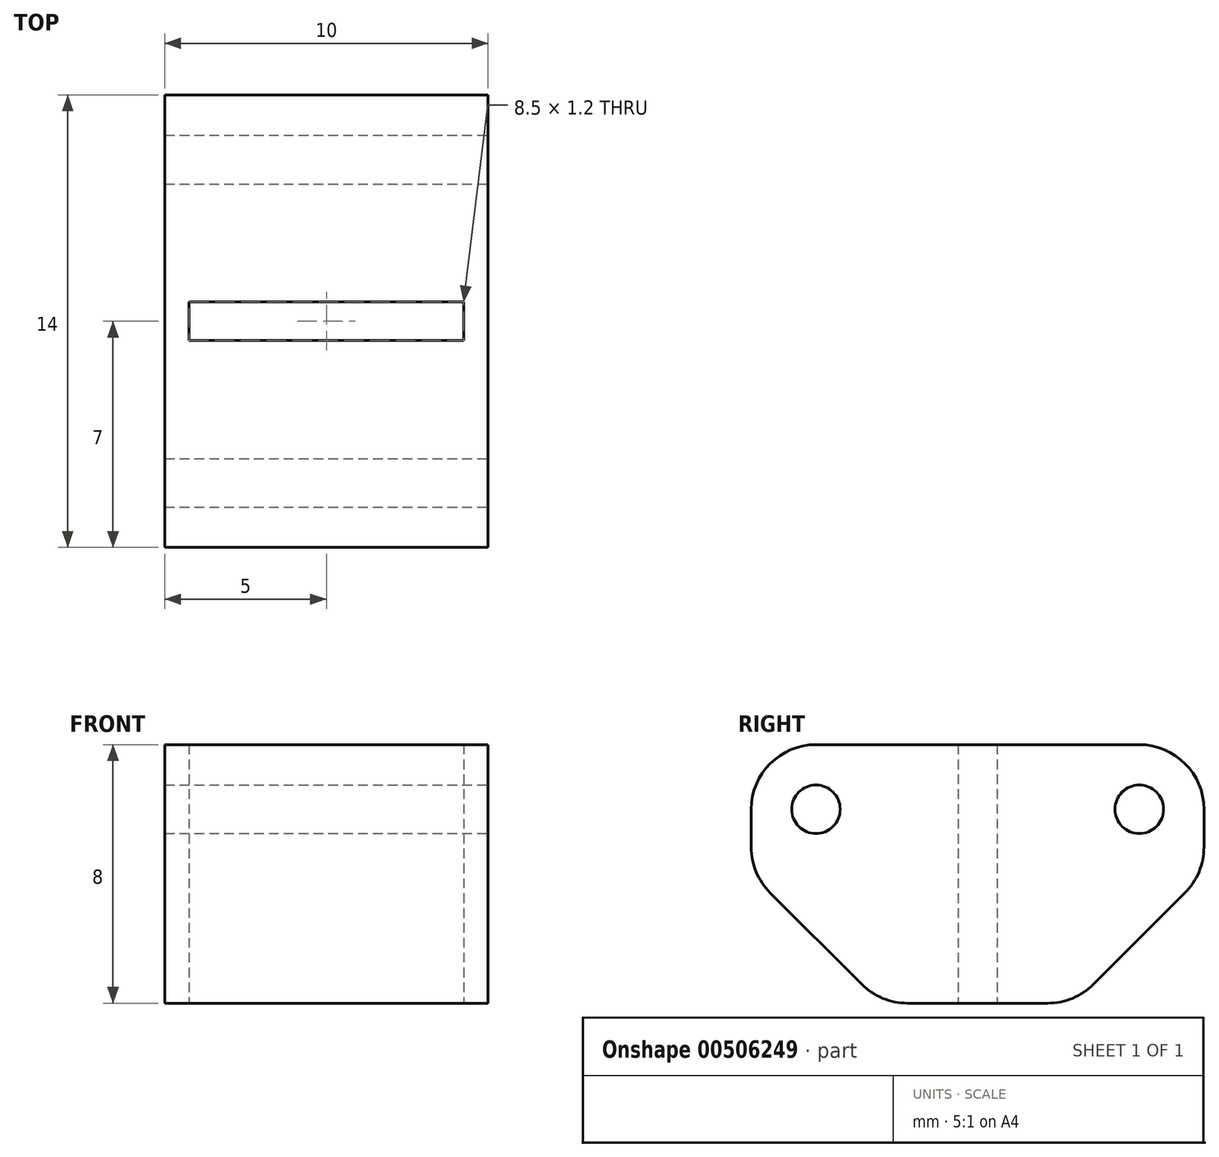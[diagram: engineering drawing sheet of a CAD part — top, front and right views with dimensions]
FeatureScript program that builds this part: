
annotation { "Feature Type Name" : "Feature", "Feature Type Description" : "" }
export const myFeature = defineFeature(function(context is Context, id is Id, definition is map)
    precondition{}
    {
        {
            var Q0;
            Q0=qCreatedBy(makeId("Top.planeOp"),FACE);
            var sketch = newSketch(context, id + "F0", { "sketchPlane" : qUnion([Q0])});
            skLineSegment(sketch, "E0.bottom", {"start": v(-5, 3) * mm, "end": v(5, 3) * mm});
            skLineSegment(sketch, "E0.top", {"start": v(-5, -3) * mm, "end": v(5, -3) * mm});
            skLineSegment(sketch, "E0.left", {"start": v(-5, 3) * mm, "end": v(-5, -3) * mm});
            skLineSegment(sketch, "E0.right", {"start": v(5, 3) * mm, "end": v(5, -3) * mm});
            skLineSegment(sketch, "E1.bottom", {"start": v(-4.25, 0.6) * mm, "end": v(4.25, 0.6) * mm});
            skLineSegment(sketch, "E1.top", {"start": v(-4.25, -0.6) * mm, "end": v(4.25, -0.6) * mm});
            skLineSegment(sketch, "E1.left", {"start": v(-4.25, 0.6) * mm, "end": v(-4.25, -0.6) * mm});
            skLineSegment(sketch, "E1.right", {"start": v(4.25, 0.6) * mm, "end": v(4.25, -0.6) * mm});
            skSolve(sketch);
        }
        {
            var Q0;
            Q0=makeQuery(id+"F0.imprint","IMPRINT",FACE,{"disambiguationData":[TD([[makeQuery(id+"F0.imprint","IMPRINT",EDGE,{"derivedFrom":sQuery(id+"F0.wireOp",EDGE,"E0.bottom")}),-1.0]])]});
            extrude(context, id + "F1", {"entities" : qUnion([Q0]), "depth" : 8 * mm});
        }
        {
            var Q0;
            Q0=makeQuery(id+"F1.opExtrude","SWEPT_FACE",FACE,{"disambiguationData":[OSD([sQuery(id+"F0.wireOp",EDGE,"E0.right")])]});
            var sketch = newSketch(context, id + "F2", { "sketchPlane" : qUnion([Q0])});
            skLineSegment(sketch, "E2.left", {"start": v(-3, 8) * mm, "end": v(-3, 8) * mm});
            skLineSegment(sketch, "E3.bottom", {"start": v(-3, 8) * mm, "end": v(-5, 8) * mm});
            skLineSegment(sketch, "E3.top", {"start": v(-3, 4) * mm, "end": v(-7, 4) * mm});
            skLineSegment(sketch, "E3.left", {"start": v(-3, 8) * mm, "end": v(-3, 4) * mm});
            skLineSegment(sketch, "E3.right", {"start": v(-7, 6) * mm, "end": v(-7, 4) * mm});
            skCircle(sketch, "E4", {"center": v(-5, 6) * mm, "radius": 0.75 * mm});
            skLineSegment(sketch, "E5.bottom", {"start": v(3, 8) * mm, "end": v(5, 8) * mm});
            skLineSegment(sketch, "E5.top", {"start": v(3, 4) * mm, "end": v(7, 4) * mm});
            skLineSegment(sketch, "E5.left", {"start": v(3, 8) * mm, "end": v(3, 4) * mm});
            skLineSegment(sketch, "E5.right", {"start": v(7, 6) * mm, "end": v(7, 4) * mm});
            skCircle(sketch, "E6", {"center": v(5, 6) * mm, "radius": 0.75 * mm});
            skPoint(sketch, "E7.visualSharp", {"position": v(-7, 8) * mm});
            skArc(sketch, "E7.filletArc", {"start": v(-5, 8) * mm, "mid": v(-6.41, 7.41) * mm, "end": v(-7, 6) * mm});
            skLineSegment(sketch, "E8", {"start": v(-7, 4) * mm, "end": v(-3, 0) * mm});
            skLineSegment(sketch, "E9", {"start": v(7, 4) * mm, "end": v(3, 0) * mm});
            skPoint(sketch, "E10.visualSharp", {"position": v(7, 8) * mm});
            skArc(sketch, "E10.filletArc", {"start": v(7, 6) * mm, "mid": v(6.41, 7.41) * mm, "end": v(5, 8) * mm});
            skSolve(sketch);
        }
        {
            var Q0;
            Q0=makeQuery(id+"F2.imprint","IMPRINT",FACE,{"disambiguationData":[TD([[makeQuery(id+"F2.imprint","IMPRINT",EDGE,{"derivedFrom":sQuery(id+"F2.wireOp",EDGE,"E3.bottom")}),1.0]])]});
            var Q1;
            {var subQ0=sQuery(id+"F2.wireOp",EDGE,"E3.top");Q1=makeQuery(id+"F2.imprint","IMPRINT",FACE,{"disambiguationData":[TD([[makeQuery(id+"F2.imprint","IMPRINT",EDGE,{"derivedFrom":subQ0}),1.0]])]});}
            var Q2;
            Q2=makeQuery(id+"F2.imprint","IMPRINT",FACE,{"disambiguationData":[TD([[makeQuery(id+"F2.imprint","IMPRINT",EDGE,{"derivedFrom":sQuery(id+"F2.wireOp",EDGE,"E5.bottom")}),-1.0]])]});
            var Q3;
            {var subQ0=sQuery(id+"F2.wireOp",EDGE,"E5.top");Q3=makeQuery(id+"F2.imprint","IMPRINT",FACE,{"disambiguationData":[TD([[makeQuery(id+"F2.imprint","IMPRINT",EDGE,{"derivedFrom":subQ0}),-1.0]])]});}
            extrude(context, id + "F3", {"entities" : qUnion([Q0, Q1, Q2, Q3]), "oppositeDirection" : true, "depth" : 10 * mm});
        }
        {
            var Q0;
            Q0=makeQuery(id+"F1.opExtrude","SWEPT_BODY",BODY,{"disambiguationData":[OSD([sQuery(id+"F0.wireOp",EDGE,"E0.bottom"),sQuery(id+"F0.wireOp",EDGE,"E0.top"),sQuery(id+"F0.wireOp",EDGE,"E0.left"),sQuery(id+"F0.wireOp",EDGE,"E0.right"),sQuery(id+"F0.wireOp",EDGE,"E1.bottom"),sQuery(id+"F0.wireOp",EDGE,"E1.top"),sQuery(id+"F0.wireOp",EDGE,"E1.left"),sQuery(id+"F0.wireOp",EDGE,"E1.right")])]});
            var Q1;
            Q1=makeQuery(id+"F3.opExtrude","SWEPT_BODY",BODY,{"disambiguationData":[OSD([sQuery(id+"F0.wireOp",EDGE,"E0.top"),sQuery(id+"F0.wireOp",EDGE,"E0.right"),sQuery(id+"F2.wireOp",EDGE,"E3.bottom"),sQuery(id+"F2.wireOp",EDGE,"E3.left"),sQuery(id+"F2.wireOp",EDGE,"E3.right"),sQuery(id+"F2.wireOp",EDGE,"E4"),sQuery(id+"F2.wireOp",EDGE,"E7.filletArc"),sQuery(id+"F2.wireOp",EDGE,"E8")])]});
            var Q2;
            Q2=makeQuery(id+"F3.opExtrude","SWEPT_BODY",BODY,{"disambiguationData":[OSD([sQuery(id+"F0.wireOp",EDGE,"E0.bottom"),sQuery(id+"F0.wireOp",EDGE,"E0.right"),sQuery(id+"F2.wireOp",EDGE,"E5.bottom"),sQuery(id+"F2.wireOp",EDGE,"E5.left"),sQuery(id+"F2.wireOp",EDGE,"E5.right"),sQuery(id+"F2.wireOp",EDGE,"E6"),sQuery(id+"F2.wireOp",EDGE,"E9"),sQuery(id+"F2.wireOp",EDGE,"E10.filletArc")])]});
            booleanBodies(context, id + "F4", {"operationType" : BooleanOperationType.UNION, "tools" : qUnion([Q0, Q1, Q2])});
        }
        {
            var Q0;
            {var subQ0=sQuery(id+"F0.wireOp",EDGE,"E0.bottom");Q0=makeQuery(id+"F4.opBoolean","MERGE",EDGE,{"derivedFrom":[makeQuery(id+"F1.opExtrude","CAP_EDGE",EDGE,{"disambiguationData":[OSD([subQ0])],"isStart":true}),makeQuery(id+"F3.opExtrude","SWEPT_EDGE",EDGE,{"disambiguationData":[OSD([subQ0,sQuery(id+"F0.wireOp",EDGE,"E0.right"),sQuery(id+"F2.wireOp",EDGE,"E9")])]})]});}
            var Q1;
            Q1=makeQuery(id+"F3.opExtrude","SWEPT_EDGE",EDGE,{"disambiguationData":[OSD([sQuery(id+"F2.wireOp",EDGE,"E5.top"),sQuery(id+"F2.wireOp",EDGE,"E5.right"),sQuery(id+"F2.wireOp",EDGE,"E9")])]});
            var Q2;
            {var subQ0=sQuery(id+"F0.wireOp",EDGE,"E0.top");Q2=makeQuery(id+"F4.opBoolean","MERGE",EDGE,{"derivedFrom":[makeQuery(id+"F1.opExtrude","CAP_EDGE",EDGE,{"disambiguationData":[OSD([subQ0])],"isStart":true}),makeQuery(id+"F3.opExtrude","SWEPT_EDGE",EDGE,{"disambiguationData":[OSD([subQ0,sQuery(id+"F0.wireOp",EDGE,"E0.right"),sQuery(id+"F2.wireOp",EDGE,"E8")])]})]});}
            var Q3;
            Q3=makeQuery(id+"F3.opExtrude","SWEPT_EDGE",EDGE,{"disambiguationData":[OSD([sQuery(id+"F2.wireOp",EDGE,"E3.top"),sQuery(id+"F2.wireOp",EDGE,"E3.right"),sQuery(id+"F2.wireOp",EDGE,"E8")])]});
            fillet(context, id + "F5", {"entities" : qUnion([Q0, Q1, Q2, Q3]), "radius" : 2 * mm, "tangentPropagation" : true, "allowEdgeOverflow" : false});
        }
    });
